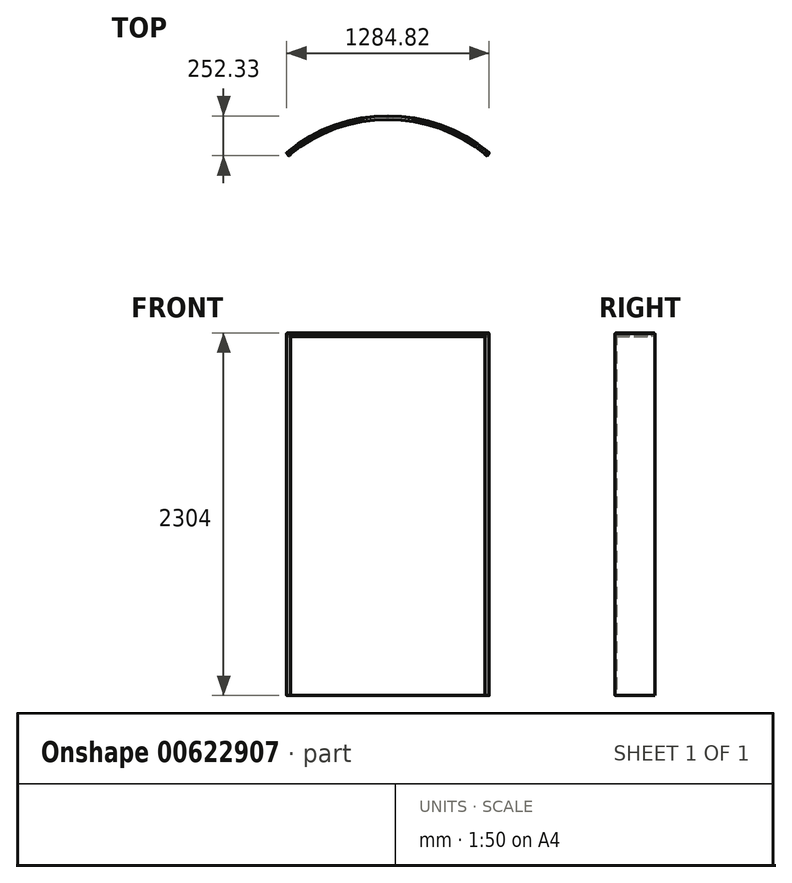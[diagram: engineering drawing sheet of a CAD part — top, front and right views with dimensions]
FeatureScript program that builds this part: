
annotation { "Feature Type Name" : "Feature", "Feature Type Description" : "" }
export const myFeature = defineFeature(function(context is Context, id is Id, definition is map)
    precondition{}
    {
        {
            var Q0;
            Q0=qCreatedBy(makeId("Top.planeOp"),FACE);
            var sketch = newSketch(context, id + "F0", { "sketchPlane" : qUnion([Q0])});
            skLineSegment(sketch, "E0", {"start": v(0, 0) * mm, "end": v(0, 1000) * mm, "construction": true});
            skLineSegment(sketch, "E1", {"start": v(-641.02, 763.93) * mm, "end": v(-629.45, 750.15) * mm, "construction": true});
            skLineSegment(sketch, "E2", {"start": v(-625.58, 749.81) * mm, "end": v(-617.72, 756.4) * mm, "construction": true});
            skLineSegment(sketch, "E3.MirrorCS", {"start": v(625.58, 749.81) * mm, "end": v(617.72, 756.4) * mm, "construction": true});
            skLineSegment(sketch, "E4.MirrorCS", {"start": v(641.02, 763.93) * mm, "end": v(629.45, 750.15) * mm, "construction": true});
            skArc(sketch, "E5.MirrorCS", {"start": v(640.67, 767.81) * mm, "mid": v(0, 1000) * mm, "end": v(-640.67, 767.81) * mm, "construction": true});
            skPoint(sketch, "E6.visualSharp", {"position": v(-642.79, 766.04) * mm});
            skArc(sketch, "E6.filletArc", {"start": v(-640.67, 767.81) * mm, "mid": v(-641.65, 765.95) * mm, "end": v(-641.02, 763.93) * mm, "construction": true});
            skPoint(sketch, "E7.visualSharp", {"position": v(-627.68, 748.04) * mm});
            skArc(sketch, "E7.filletArc", {"start": v(-629.45, 750.15) * mm, "mid": v(-627.58, 749.18) * mm, "end": v(-625.58, 749.81) * mm, "construction": true});
            skPoint(sketch, "E8.visualSharp", {"position": v(627.68, 748.04) * mm});
            skArc(sketch, "E8.filletArc", {"start": v(625.58, 749.81) * mm, "mid": v(627.58, 749.18) * mm, "end": v(629.45, 750.15) * mm, "construction": true});
            skPoint(sketch, "E9.visualSharp", {"position": v(642.79, 766.04) * mm});
            skArc(sketch, "E9.filletArc", {"start": v(641.02, 763.93) * mm, "mid": v(641.65, 765.95) * mm, "end": v(640.67, 767.81) * mm, "construction": true});
            skLineSegment(sketch, "E10.0", {"start": v(-625.1, 749.24) * mm, "end": v(-617.24, 755.82) * mm});
            skArc(sketch, "E10.1", {"start": v(-630.02, 749.67) * mm, "mid": v(-627.65, 748.43) * mm, "end": v(-625.1, 749.24) * mm});
            skLineSegment(sketch, "E10.2", {"start": v(-641.6, 763.45) * mm, "end": v(-630.02, 749.67) * mm});
            skArc(sketch, "E10.3", {"start": v(-641.15, 768.39) * mm, "mid": v(-642.4, 766.01) * mm, "end": v(-641.6, 763.45) * mm});
            skArc(sketch, "E10.4", {"start": v(641.15, 768.39) * mm, "mid": v(0, 1000.75) * mm, "end": v(-641.15, 768.39) * mm});
            skLineSegment(sketch, "E10.5", {"start": v(625.1, 749.24) * mm, "end": v(617.24, 755.82) * mm});
            skArc(sketch, "E10.6", {"start": v(625.1, 749.24) * mm, "mid": v(627.65, 748.43) * mm, "end": v(630.02, 749.67) * mm});
            skLineSegment(sketch, "E10.7", {"start": v(641.6, 763.45) * mm, "end": v(630.02, 749.67) * mm});
            skArc(sketch, "E10.8", {"start": v(641.6, 763.45) * mm, "mid": v(642.4, 766.01) * mm, "end": v(641.15, 768.39) * mm});
            skLineSegment(sketch, "E11.0", {"start": v(-626.06, 750.38) * mm, "end": v(-618.2, 756.97) * mm});
            skLineSegment(sketch, "E11.1", {"start": v(626.06, 750.38) * mm, "end": v(618.2, 756.97) * mm});
            skLineSegment(sketch, "E11.2", {"start": v(640.44, 764.42) * mm, "end": v(628.88, 750.63) * mm});
            skArc(sketch, "E11.3", {"start": v(640.2, 767.24) * mm, "mid": v(0, 999.25) * mm, "end": v(-640.2, 767.24) * mm});
            skLineSegment(sketch, "E11.4", {"start": v(-640.44, 764.42) * mm, "end": v(-628.88, 750.63) * mm});
            skPoint(sketch, "E12.visualSharp", {"position": v(-627.59, 749.1) * mm});
            skArc(sketch, "E12.filletArc", {"start": v(-628.88, 750.63) * mm, "mid": v(-627.52, 749.92) * mm, "end": v(-626.06, 750.38) * mm});
            skPoint(sketch, "E13.visualSharp", {"position": v(627.59, 749.1) * mm});
            skArc(sketch, "E13.filletArc", {"start": v(626.06, 750.38) * mm, "mid": v(627.52, 749.92) * mm, "end": v(628.88, 750.63) * mm});
            skPoint(sketch, "E14.visualSharp", {"position": v(-641.73, 765.95) * mm});
            skArc(sketch, "E14.filletArc", {"start": v(-640.2, 767.24) * mm, "mid": v(-640.9, 765.88) * mm, "end": v(-640.44, 764.42) * mm});
            skPoint(sketch, "E15.visualSharp", {"position": v(641.73, 765.95) * mm});
            skArc(sketch, "E15.filletArc", {"start": v(640.44, 764.42) * mm, "mid": v(640.9, 765.88) * mm, "end": v(640.2, 767.24) * mm});
            skLineSegment(sketch, "E16", {"start": v(-618.2, 756.97) * mm, "end": v(-617.24, 755.82) * mm});
            skLineSegment(sketch, "E17", {"start": v(617.24, 755.82) * mm, "end": v(618.2, 756.97) * mm});
            skSolve(sketch);
        }
        {
            var Q0;
            Q0=makeQuery(id+"F0.imprint","IMPRINT",FACE,{"disambiguationData":[TD([[makeQuery(id+"F0.imprint","IMPRINT",EDGE,{"derivedFrom":sQuery(id+"F0.wireOp",EDGE,"E10.0")}),1.0]])]});
            var Q1;
            Q1 = qConstructionFilter(qBodyType(qCreatedBy(id + "F0" ,EDGE), BodyType.WIRE), ConstructionObject.NO);
            extrude(context, id + "F1", {"entities" : qUnion([Q0]), "surfaceEntities" : qUnion([Q1]), "endBound" : BoundingType.SYMMETRIC, "depth" : 2300 * mm, "offsetDistance" : 25 * mm});
        }
        {
            var Q0;
            Q0=qCreatedBy(makeId("Right.planeOp"),FACE);
            var sketch = newSketch(context, id + "F2", { "sketchPlane" : qUnion([Q0])});
            skLineSegment(sketch, "E18.bottom", {"start": v(983.25, 1154) * mm, "end": v(995.25, 1154) * mm});
            skLineSegment(sketch, "E18.top", {"start": v(983.25, 1132) * mm, "end": v(995.25, 1132) * mm});
            skLineSegment(sketch, "E18.left", {"start": v(979.25, 1150) * mm, "end": v(979.25, 1136) * mm});
            skLineSegment(sketch, "E18.right", {"start": v(999.25, 1150) * mm, "end": v(999.25, 1136) * mm});
            skPoint(sketch, "E19.visualSharp", {"position": v(979.25, 1154) * mm});
            skArc(sketch, "E19.filletArc", {"start": v(983.25, 1154) * mm, "mid": v(980.42, 1152.83) * mm, "end": v(979.25, 1150) * mm});
            skPoint(sketch, "E20.visualSharp", {"position": v(999.25, 1154) * mm});
            skArc(sketch, "E20.filletArc", {"start": v(999.25, 1150) * mm, "mid": v(998.08, 1152.83) * mm, "end": v(995.25, 1154) * mm});
            skPoint(sketch, "E21.visualSharp", {"position": v(999.25, 1132) * mm});
            skArc(sketch, "E21.filletArc", {"start": v(995.25, 1132) * mm, "mid": v(998.08, 1133.17) * mm, "end": v(999.25, 1136) * mm});
            skPoint(sketch, "E22.visualSharp", {"position": v(979.25, 1132) * mm});
            skArc(sketch, "E22.filletArc", {"start": v(979.25, 1136) * mm, "mid": v(980.42, 1133.17) * mm, "end": v(983.25, 1132) * mm});
            skLineSegment(sketch, "E23.0", {"start": v(983.25, 1152) * mm, "end": v(995.25, 1152) * mm});
            skLineSegment(sketch, "E23.1", {"start": v(981.25, 1150) * mm, "end": v(981.25, 1136) * mm});
            skLineSegment(sketch, "E23.2", {"start": v(983.25, 1134) * mm, "end": v(995.25, 1134) * mm});
            skLineSegment(sketch, "E23.3", {"start": v(997.25, 1150) * mm, "end": v(997.25, 1136) * mm});
            skPoint(sketch, "E24.visualSharp", {"position": v(981.25, 1152) * mm});
            skArc(sketch, "E24.filletArc", {"start": v(983.25, 1152) * mm, "mid": v(981.84, 1151.41) * mm, "end": v(981.25, 1150) * mm});
            skPoint(sketch, "E25.visualSharp", {"position": v(997.25, 1152) * mm});
            skArc(sketch, "E25.filletArc", {"start": v(997.25, 1150) * mm, "mid": v(996.66, 1151.41) * mm, "end": v(995.25, 1152) * mm});
            skPoint(sketch, "E26.visualSharp", {"position": v(997.25, 1134) * mm});
            skArc(sketch, "E26.filletArc", {"start": v(995.25, 1134) * mm, "mid": v(996.66, 1134.59) * mm, "end": v(997.25, 1136) * mm});
            skPoint(sketch, "E27.visualSharp", {"position": v(981.25, 1134) * mm});
            skArc(sketch, "E27.filletArc", {"start": v(981.25, 1136) * mm, "mid": v(981.84, 1134.59) * mm, "end": v(983.25, 1134) * mm});
            skSolve(sketch);
        }
        {
            var Q0;
            Q0=makeQuery(id+"F1.opExtrude","CAP_FACE",FACE,{"disambiguationData":[OSD([sQuery(id+"F0.wireOp",EDGE,"E10.0"),sQuery(id+"F0.wireOp",EDGE,"E10.1"),sQuery(id+"F0.wireOp",EDGE,"E10.2"),sQuery(id+"F0.wireOp",EDGE,"E10.3"),sQuery(id+"F0.wireOp",EDGE,"E10.4"),sQuery(id+"F0.wireOp",EDGE,"E10.5"),sQuery(id+"F0.wireOp",EDGE,"E10.6"),sQuery(id+"F0.wireOp",EDGE,"E10.7"),sQuery(id+"F0.wireOp",EDGE,"E10.8"),sQuery(id+"F0.wireOp",EDGE,"E11.0"),sQuery(id+"F0.wireOp",EDGE,"E11.1"),sQuery(id+"F0.wireOp",EDGE,"E11.2"),sQuery(id+"F0.wireOp",EDGE,"E11.3"),sQuery(id+"F0.wireOp",EDGE,"E11.4"),sQuery(id+"F0.wireOp",EDGE,"E12.filletArc"),sQuery(id+"F0.wireOp",EDGE,"E13.filletArc"),sQuery(id+"F0.wireOp",EDGE,"E14.filletArc"),sQuery(id+"F0.wireOp",EDGE,"E15.filletArc"),sQuery(id+"F0.wireOp",EDGE,"E16"),sQuery(id+"F0.wireOp",EDGE,"E17")])],"isStart":false});
            var sketch = newSketch(context, id + "F3", { "sketchPlane" : qUnion([Q0])});
            skArc(sketch, "E28.0", {"start": v(640.2, 767.24) * mm, "mid": v(0, 999.25) * mm, "end": v(-640.2, 767.24) * mm});
            skSolve(sketch);
        }
        {
            var Q0;
            Q0 = qSketchRegion(id + "F2", true);
            var Q1;
            Q1=sQuery(id+"F3.wireOp",EDGE,"E28.0");
            sweep(context, id + "F4", {"operationType" : NewBodyOperationType.ADD, "profiles" : qUnion([Q0]), "path" : qUnion([Q1])});
        }
    });
